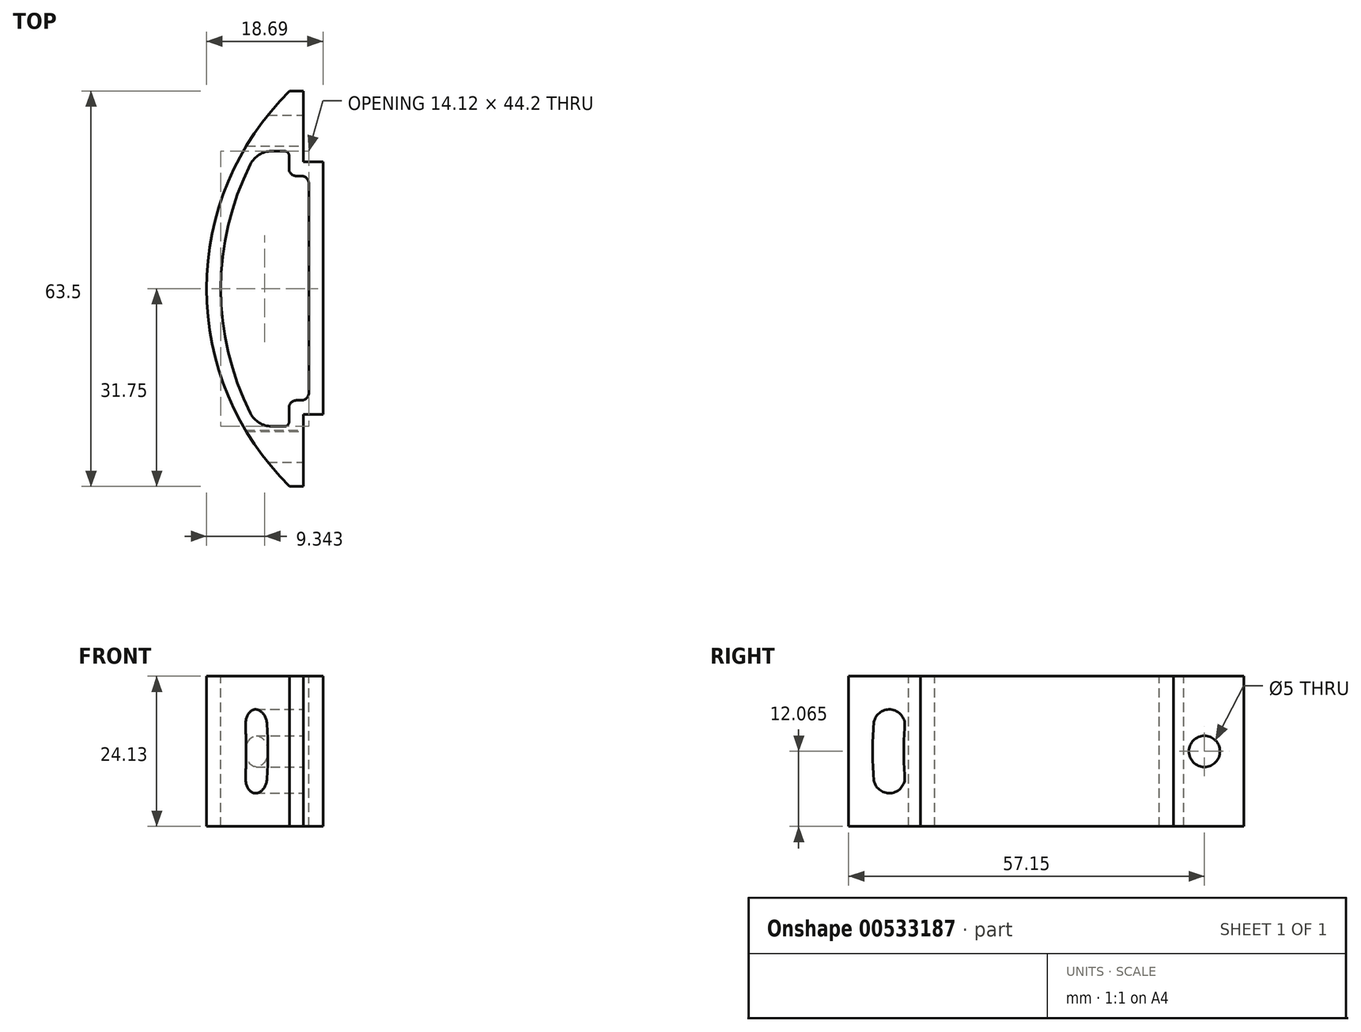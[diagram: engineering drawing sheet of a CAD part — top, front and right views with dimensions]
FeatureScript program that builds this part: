
annotation { "Feature Type Name" : "Feature", "Feature Type Description" : "" }
export const myFeature = defineFeature(function(context is Context, id is Id, definition is map)
    precondition{}
    {
        {
            var Q0;
            Q0=qCreatedBy(makeId("Top.planeOp"),FACE);
            var sketch = newSketch(context, id + "F0", { "sketchPlane" : qUnion([Q0])});
            skLineSegment(sketch, "E0", {"start": v(-22.07, 31.75) * mm, "end": v(-22.07, -31.75) * mm});
            skLineSegment(sketch, "E1", {"start": v(-22.07, -31.75) * mm, "end": v(-24.24, -31.75) * mm});
            skLineSegment(sketch, "E2", {"start": v(-22.07, 31.75) * mm, "end": v(-24.24, 31.75) * mm});
            skPoint(sketch, "E3", {"position": v(-22.07, 0) * mm});
            skArc(sketch, "E4", {"start": v(-24.24, 31.75) * mm, "mid": v(-37.58, 0) * mm, "end": v(-24.24, -31.75) * mm});
            skSolve(sketch);
        }
        {
            var Q0;
            Q0=makeQuery(id+"F0.imprint","IMPRINT",FACE,{"disambiguationData":[TD([[makeQuery(id+"F0.imprint","IMPRINT",EDGE,{"derivedFrom":sQuery(id+"F0.wireOp",EDGE,"ZQ69L5l8-Qg1F-rpHX-hbtI-eBNDKVVa1CUx")}),1.0]])]});
            var Q1;
            Q1=makeQuery(id+"F0.imprint","IMPRINT",FACE,{"disambiguationData":[TD([[makeQuery(id+"F0.imprint","IMPRINT",EDGE,{"derivedFrom":sQuery(id+"F0.wireOp",EDGE,"E0")}),-1.0]])]});
            extrude(context, id + "F1", {"entities" : qUnion([Q0, Q1]), "depth" : 24.13 * mm, "offsetDistance" : 25.4 * mm});
        }
        {
            var Q0;
            Q0=makeQuery(id+"F1.opExtrude","SWEPT_FACE",FACE,{"disambiguationData":[OSD([sQuery(id+"F0.wireOp",EDGE,"E0")])]});
            var sketch = newSketch(context, id + "F2", { "sketchPlane" : qUnion([Q0])});
            skLineSegment(sketch, "E5", {"start": v(-31.75, 19.69) * mm, "end": v(-31.75, 4.45) * mm});
            skPoint(sketch, "E6", {"position": v(-31.75, 12.07) * mm});
            skLineSegment(sketch, "E7", {"start": v(-31.75, 12.07) * mm, "end": v(26.83, 12.07) * mm});
            skPoint(sketch, "E8", {"position": v(-25.4, 12.07) * mm});
            skPoint(sketch, "E9", {"position": v(25.4, 12.07) * mm});
            skArc(sketch, "E10", {"start": v(-22.73, 16.09) * mm, "mid": v(-25.02, 18.79) * mm, "end": v(-27.72, 16.5) * mm});
            skArc(sketch, "E11.MirrorCS", {"start": v(-22.73, 8.04) * mm, "mid": v(-25.02, 5.34) * mm, "end": v(-27.72, 7.62) * mm});
            skPoint(sketch, "E12.MirrorCS.end.orphan", {"position": v(-27.88, 12.07) * mm});
            skPoint(sketch, "E12.MirrorCS.start.orphan", {"position": v(-44.28, 25.45) * mm});
            skPoint(sketch, "E13.MirrorCS.end.orphan", {"position": v(-22.88, 12.07) * mm});
            skPoint(sketch, "E13.MirrorCS.start.orphan", {"position": v(-22.73, 8.04) * mm});
            skArc(sketch, "E14", {"start": v(-22.73, 16.09) * mm, "mid": v(-22.9, 12.07) * mm, "end": v(-22.73, 8.04) * mm});
            skArc(sketch, "E15", {"start": v(-27.72, 16.5) * mm, "mid": v(-27.9, 12.06) * mm, "end": v(-27.72, 7.62) * mm});
            skSolve(sketch);
        }
        {
            var Q0;
            Q0 = qSketchRegion(id + "F2", true);
            extrude(context, id + "F3", {"entities" : qUnion([Q0]), "operationType" : NewBodyOperationType.REMOVE, "oppositeDirection" : true, "depth" : 25.4 * mm, "offsetDistance" : 25.4 * mm});
        }
        {
            var Q0;
            Q0=sQuery(id+"F2.wireOp",VERTEX,"E9");
            var Q1;
            Q1=makeQuery(id+"F1.opExtrude","SWEPT_BODY",BODY,{"disambiguationData":[OSD([sQuery(id+"F0.wireOp",EDGE,"ZQ69L5l8-Qg1F-rpHX-hbtI-eBNDKVVa1CUx"),sQuery(id+"F0.wireOp",EDGE,"E0"),sQuery(id+"F0.wireOp",EDGE,"E1"),sQuery(id+"F0.wireOp",EDGE,"E2")])]});
            hole(context, id + "F4", {"style" : HoleStyle.SIMPLE, "endStyle" : HoleEndStyle.BLIND, "standardTappedOrClearance" : lookupTablePath({ "standard" : "ISO", "engagement" : "75%", "pitch" : "1 mm", "size" : "M6", "type" : "Tapped" }), "standardBlindInLast" : lookupTablePath({ "standard" : "ISO", "engagement" : "75%", "pitch" : "1 mm", "size" : "M6", "type" : "Tapped" }), "holeDiameter" : 5 * mm, "showTappedDepth" : true, "holeDepth" : 15.7 * mm, "isTappedThrough" : true, "tappedDepth" : 12.7 * mm, "tapClearance" : 3, "locations" : qUnion([Q0]), "scope" : qUnion([Q1]), "majorDiameter" : 6 * mm});
        }
        {
            var Q0;
            {var subQ6=sQuery(id+"F2.wireOp",EDGE,"E10");Q0=makeQuery(id+"F2.imprint","IMPRINT",FACE,{"disambiguationData":[TD([[makeQuery(id+"F2.imprint","IMPRINT",EDGE,{"derivedFrom":subQ6}),-1.0]])]});}
            var sketch = newSketch(context, id + "F5", { "sketchPlane" : qUnion([Q0])});
            skLineSegment(sketch, "E16.bottom", {"start": v(-20.22, 24.13) * mm, "end": v(18.85, 24.13) * mm});
            skLineSegment(sketch, "E16.top", {"start": v(-20.22, 0) * mm, "end": v(18.85, 0) * mm});
            skLineSegment(sketch, "E16.left", {"start": v(-20.22, 24.13) * mm, "end": v(-20.22, 0) * mm});
            skLineSegment(sketch, "E17.bottom", {"start": v(20.4, 24.13) * mm, "end": v(18.85, 24.13) * mm});
            skLineSegment(sketch, "E17.left", {"start": v(20.4, 24.13) * mm, "end": v(20.4, 0) * mm});
            skPoint(sketch, "E18", {"position": v(-25.22, 16.3) * mm});
            skPoint(sketch, "E19", {"position": v(-25.22, 7.83) * mm});
            skPoint(sketch, "E20", {"position": v(25.4, 12.07) * mm});
            skLineSegment(sketch, "E21.bottom", {"start": v(18.85, 0) * mm, "end": v(20.4, 0) * mm});
            skLineSegment(sketch, "E21.right", {"start": v(20.4, 0) * mm, "end": v(20.4, 0) * mm});
            skSolve(sketch);
        }
        {
            var Q0;
            Q0=makeQuery(id+"F5.imprint","IMPRINT",FACE,{"disambiguationData":[TD([[makeQuery(id+"F5.imprint","IMPRINT",EDGE,{"derivedFrom":sQuery(id+"F5.wireOp",EDGE,"E16.bottom")}),-1.0]])]});
            var Q1;
            Q1=makeQuery(id+"F5.imprint","IMPRINT",FACE,{"disambiguationData":[TD([[makeQuery(id+"F5.imprint","IMPRINT",EDGE,{"derivedFrom":sQuery(id+"F5.wireOp",EDGE,"E17.bottom")}),1.0]])]});
            extrude(context, id + "F6", {"entities" : qUnion([Q0, Q1]), "operationType" : NewBodyOperationType.ADD, "depth" : 3.17 * mm, "offsetDistance" : 25.4 * mm});
        }
        {
            var Q0;
            Q0=makeQuery(id+"F6.boolean.opBoolean","MERGE",FACE,{"derivedFrom":[makeQuery(id+"F1.opExtrude","CAP_FACE",FACE,{"disambiguationData":[OSD([sQuery(id+"F0.wireOp",EDGE,"E0"),sQuery(id+"F0.wireOp",EDGE,"E1"),sQuery(id+"F0.wireOp",EDGE,"E2"),sQuery(id+"F0.wireOp",EDGE,"E4")])],"isStart":false}),makeQuery(id+"F6.opExtrude","SWEPT_FACE",FACE,{"disambiguationData":[OSD([sQuery(id+"F5.wireOp",EDGE,"E16.bottom"),sQuery(id+"F5.wireOp",EDGE,"E17.bottom")])]})]});
            cPlane(context, id + "F7", {"entities" : qUnion([Q0]), "cplaneType" : CPlaneType.OFFSET, "offset" : 0 * mm, "width" : 152.4 * mm, "height" : 152.4 * mm});
        }
        {
            var Q0;
            Q0=qCreatedBy(id+"F7.planeOp",FACE);
            var sketch = newSketch(context, id + "F8", { "sketchPlane" : qUnion([Q0])});
            skLineSegment(sketch, "E22.bottom", {"start": v(-25.02, -22.1) * mm, "end": v(-27.14, -22.1) * mm});
            skLineSegment(sketch, "E22.top", {"start": v(-25.02, 22.1) * mm, "end": v(-27.14, 22.1) * mm});
            skLineSegment(sketch, "E22.left", {"start": v(-24.35, -21.43) * mm, "end": v(-24.35, -19.1) * mm});
            skArc(sketch, "E23", {"start": v(-30.54, 20) * mm, "mid": v(-35.3, 0) * mm, "end": v(-30.54, -20) * mm});
            skPoint(sketch, "E24.visualSharp", {"position": v(-29.41, 22.1) * mm});
            skArc(sketch, "E24.filletArc", {"start": v(-27.14, 22.1) * mm, "mid": v(-28.94, 21.64) * mm, "end": v(-30.32, 20.39) * mm});
            skPoint(sketch, "E25.visualSharp", {"position": v(-24.35, 22.1) * mm});
            skArc(sketch, "E25.filletArc", {"start": v(-24.35, 21.43) * mm, "mid": v(-24.55, 21.9) * mm, "end": v(-25.02, 22.1) * mm});
            skPoint(sketch, "E26.visualSharp", {"position": v(-24.35, -22.1) * mm});
            skArc(sketch, "E26.filletArc", {"start": v(-25.02, -22.1) * mm, "mid": v(-24.55, -21.9) * mm, "end": v(-24.35, -21.43) * mm});
            skPoint(sketch, "E27.visualSharp", {"position": v(-29.41, -22.1) * mm});
            skArc(sketch, "E27.filletArc", {"start": v(-30.41, -20.23) * mm, "mid": v(-29.02, -21.6) * mm, "end": v(-27.14, -22.1) * mm});
            skPoint(sketch, "E28.visualSharp", {"position": v(-30.54, 20) * mm});
            skArc(sketch, "E28.filletArc", {"start": v(-30.32, 20.39) * mm, "mid": v(-30.43, 20.2) * mm, "end": v(-30.54, 20) * mm});
            skPoint(sketch, "E29.visualSharp", {"position": v(-30.54, -20) * mm});
            skArc(sketch, "E29.filletArc", {"start": v(-30.54, -20) * mm, "mid": v(-30.48, -20.12) * mm, "end": v(-30.41, -20.23) * mm});
            skLineSegment(sketch, "E30.bottom", {"start": v(-23.19, -17.93) * mm, "end": v(-22.34, -17.93) * mm});
            skLineSegment(sketch, "E30.top", {"start": v(-23.19, 18.11) * mm, "end": v(-22.34, 18.11) * mm});
            skLineSegment(sketch, "E30.right", {"start": v(-21.18, -16.77) * mm, "end": v(-21.18, 16.94) * mm});
            skLineSegment(sketch, "E31.trimOffspring", {"start": v(-24.35, 19.28) * mm, "end": v(-24.35, 21.43) * mm});
            skPoint(sketch, "E32.visualSharp", {"position": v(-24.35, -17.93) * mm});
            skArc(sketch, "E32.filletArc", {"start": v(-23.19, -17.93) * mm, "mid": v(-24.01, -18.28) * mm, "end": v(-24.35, -19.1) * mm});
            skPoint(sketch, "E33.visualSharp", {"position": v(-21.18, -17.93) * mm});
            skArc(sketch, "E33.filletArc", {"start": v(-22.34, -17.93) * mm, "mid": v(-21.52, -17.6) * mm, "end": v(-21.18, -16.77) * mm});
            skPoint(sketch, "E34.visualSharp", {"position": v(-21.18, 18.11) * mm});
            skArc(sketch, "E34.filletArc", {"start": v(-21.18, 16.94) * mm, "mid": v(-21.52, 17.77) * mm, "end": v(-22.34, 18.11) * mm});
            skPoint(sketch, "E35.visualSharp", {"position": v(-24.35, 18.11) * mm});
            skArc(sketch, "E35.filletArc", {"start": v(-24.35, 19.28) * mm, "mid": v(-24.01, 18.45) * mm, "end": v(-23.19, 18.11) * mm});
            skSolve(sketch);
        }
        {
            var Q0;
            {var subQ2=sQuery(id+"F8.wireOp",EDGE,"E22.bottom");Q0=makeQuery(id+"F8.imprint","IMPRINT",FACE,{"disambiguationData":[TD([[makeQuery(id+"F8.imprint","IMPRINT",EDGE,{"derivedFrom":subQ2}),-1.0]])]});}
            extrude(context, id + "F9", {"entities" : qUnion([Q0]), "operationType" : NewBodyOperationType.REMOVE, "oppositeDirection" : true, "depth" : 25.4 * mm, "offsetDistance" : 25.4 * mm});
        }
    });
